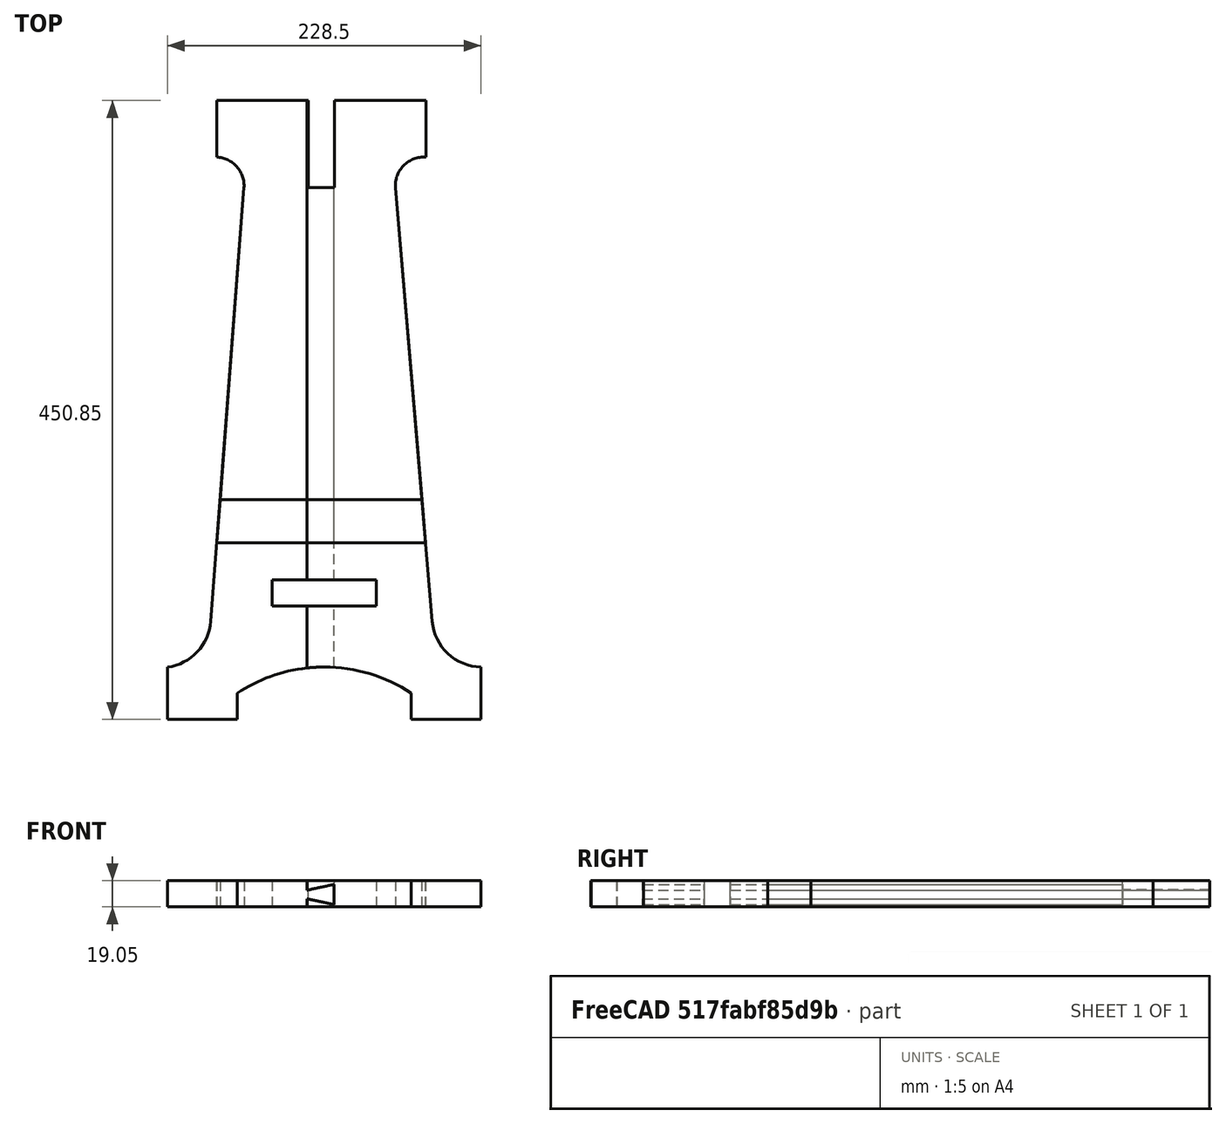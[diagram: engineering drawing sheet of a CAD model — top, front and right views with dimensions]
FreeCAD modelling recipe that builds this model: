
FCSTD DOCUMENT  (FreeCAD 0.20R29177 +426 (Git))
Label: table_test
License: All rights reserved
LicenseURL: http://en.wikipedia.org/wiki/All_rights_reserved
objects: Part::Feature×8, Part::Extrusion×3, App::Part×3, Sketcher::SketchObject×2
note: 13 computed .brp shape members not serialized (recipe doc carries the construction recipe); baked Part::Feature solids carry a one-line shape summary decoded from their .brp

FEATURE [Part::Feature] Solid003  label="vagina001"
  shape: bbox 126.8 x 450.8 x 19.05 mm, 34 faces (baked)
FEATURE [Part::Feature] Solid002  label="penis001"
  shape: bbox 121.4 x 450.9 x 19.05 mm, 29 faces (baked)
FEATURE [Part::Feature] Solid004
  shape: bbox 85.43 x 322.2 x 19.05 mm, 15 faces (baked)
FEATURE [Part::Feature] Solid005
  shape: bbox 86.66 x 322.2 x 19.05 mm, 19 faces (baked)
FEATURE [Sketcher::SketchObject] Sketch001
  FullyConstrained = false
  sketch-geometry (1):
    g0: LineSegment StartX=-133.418 StartY=-104.889 StartZ=0 EndX=51.9805 EndY=-104.889 EndZ=0
  constraints (1):
    c: Horizontal(g0)
FEATURE [Part::Extrusion] Extrude001
  Base = -> Sketch001
  Dir = (0,0,1)
  DirMode = 2
  FaceMakerClass = Part::FaceMakerBullseye
  LengthFwd = 100
  LengthRev = 0
  Placement = pos=(0,0,-30) rot=(0,0,1;0rad)
  Solid = false
  Symmetric = false
FEATURE [Part::Extrusion] Extrude002
  Base = -> Sketch001
  Dir = (0,0,1)
  DirMode = 2
  FaceMakerClass = Part::FaceMakerBullseye
  LengthFwd = 100
  LengthRev = 0
  Solid = false
  Symmetric = false
FEATURE [Part::Feature] Solid  label="vagina"
  shape: bbox 86.35 x 31.53 x 19.05 mm, 11 faces (baked)
FEATURE [Part::Feature] Solid006
  shape: bbox 86.66 x 290.6 x 19.05 mm, 19 faces (baked)
FEATURE [Part::Feature] Solid007  label="penis"
  shape: bbox 85.34 x 31.53 x 19.05 mm, 11 faces (baked)
FEATURE [Part::Feature] Solid008
  shape: bbox 85.43 x 290.6 x 19.05 mm, 15 faces (baked)
FEATURE [App::Part] Part001  label="male"
  Group = -> [Solid007]
  Origin = -> Origin001
FEATURE [App::Part] Part002  label="female"
  Group = -> [Solid]
  Origin = -> Origin002
FEATURE [App::Part] Part  label="work"
  Group = -> [Solid003,Solid002,Sketch,Extrude,Solid004,Solid005,Sketch001,Extrude001,Extrude002,Solid006,Solid008]
  Origin = -> Origin
FEATURE [Sketcher::SketchObject] Sketch
  FullyConstrained = false
  MapMode = 2
  Support = -> [Part]
  sketch-geometry (1):
    g0: LineSegment StartX=-153.603 StartY=-136.416 StartZ=0 EndX=64.0389 EndY=-136.416 EndZ=0
  constraints (1):
    c: Horizontal(g0)
FEATURE [Part::Extrusion] Extrude
  Base = -> Sketch
  Dir = (0,0,1)
  DirMode = 2
  FaceMakerClass = Part::FaceMakerBullseye
  LengthFwd = 100
  LengthRev = 0
  Placement = pos=(0,0,-41) rot=(0,0,1;0rad)
  Solid = false
  Symmetric = false
